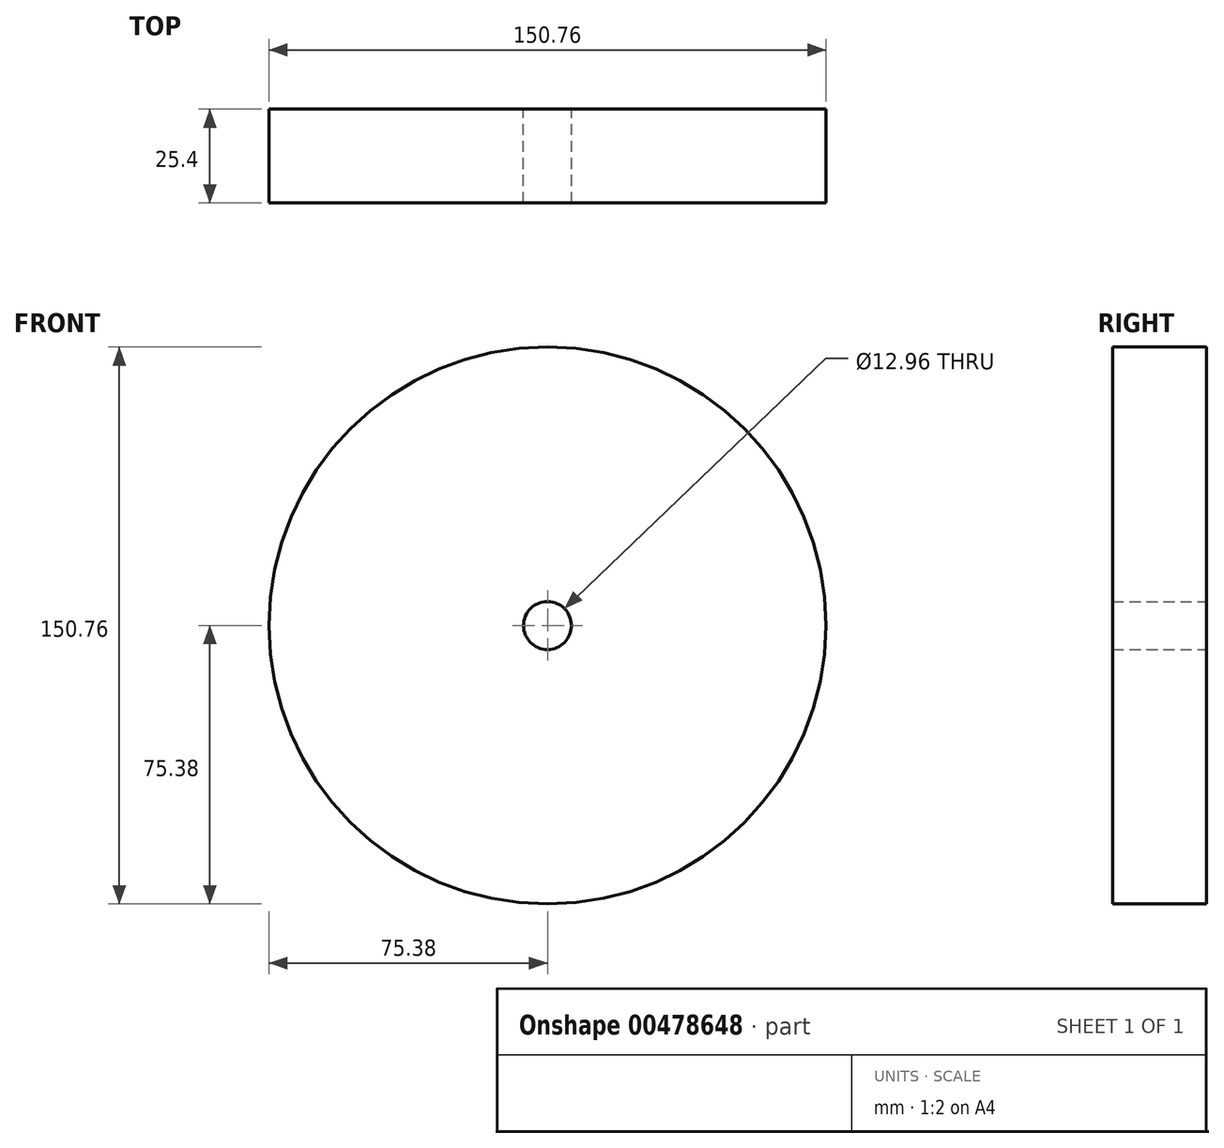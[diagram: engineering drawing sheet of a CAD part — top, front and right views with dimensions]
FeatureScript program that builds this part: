
annotation { "Feature Type Name" : "Feature", "Feature Type Description" : "" }
export const myFeature = defineFeature(function(context is Context, id is Id, definition is map)
    precondition{}
    {
        {
            var Q0;
            Q0=qCreatedBy(makeId("Front.planeOp"),FACE);
            var sketch = newSketch(context, id + "F0", { "sketchPlane" : qUnion([Q0])});
            skCircle(sketch, "E0", {"center": v(0, 0) * mm, "radius": 75.38 * mm});
            skCircle(sketch, "E1", {"center": v(0, 0) * mm, "radius": 6.48 * mm});
            skCircle(sketch, "E2", {"center": v(0, 0) * mm, "radius": 12.29 * mm});
            skCircle(sketch, "E3", {"center": v(0, 0) * mm, "radius": 60.5 * mm});
            skSolve(sketch);
        }
        {
            var Q0;
            Q0 = qSketchRegion(id + "F0", true);
            var Q1;
            Q1=makeQuery(id+"F0.imprint","IMPRINT",FACE,{"disambiguationData":[TD([[makeQuery(id+"F0.imprint","IMPRINT",EDGE,{"derivedFrom":sQuery(id+"F0.wireOp",EDGE,"E2")}),-1.0]])]});
            var Q2;
            Q2=makeQuery(id+"F0.imprint","IMPRINT",FACE,{"disambiguationData":[TD([[makeQuery(id+"F0.imprint","IMPRINT",EDGE,{"derivedFrom":sQuery(id+"F0.wireOp",EDGE,"E0")}),1.0]])]});
            var Q3;
            Q3=makeQuery(id+"F0.imprint","IMPRINT",FACE,{"disambiguationData":[TD([[makeQuery(id+"F0.imprint","IMPRINT",EDGE,{"derivedFrom":sQuery(id+"F0.wireOp",EDGE,"E1")}),-1.0]])]});
            extrude(context, id + "F1", {"entities" : qUnion([Q0, Q1, Q2, Q3]), "depth" : 25.4 * mm});
        }
    });
